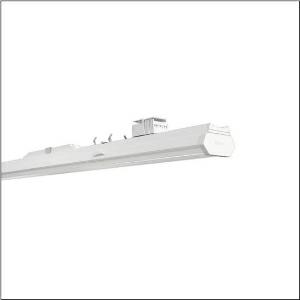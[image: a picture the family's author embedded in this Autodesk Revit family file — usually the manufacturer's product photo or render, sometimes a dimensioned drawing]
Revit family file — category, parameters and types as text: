
# Revit family: licross_r__11_protected_ho_51tp11cn4exs_0205
name_source: partatom
category: Lighting Fixtures
units: mm (PartAtom-declared; Revit-internal decimal feet)

## family parameters
Cut with Voids When Loaded = No
Host = Face
Light Source = No
Part Type = Normal
Room Calculation Point = No
Round Connector Dimension = Use Diameter
Shared = No

## types (1)
- --- (1 x LED, 14460 lm, 77.6 W, 4000K)
    Apparent Load = 78 VA
    CIE Flux Codes = 84 94 98 99 100
    Color Rendering = 80
    Color Temperature = 4000K
    Default Elevation = 1800 mm
    Description = Licross® 11 Protected HO, luminaire insert, of sheet steel, galvanised, coil coated, white, length: 1.500mm, width: 90mm, height: 101mm, LED rated luminous flux: 14.460lm, light colour: 840, control gear: ON/OFF Multilumen, CLOi, with plug, 3-pole, with phase selection, mains connection: 220..240V, AC, 50/60Hz, start of lifetime: 78W, end of service life: 87W, halogen-free wiring, primary light control with lens, of plastic, primary optical cover: cover, of PMMA, light emission: direct distribution, primary light characteristic: symmetric, protection rating (complete): IP64, insulation class (complete): insulation class I (protective earthing), certification: CE, ENEC, VDE, UKCA, protection symbol: D if used in an environment with conductive dust loads with corresponding accessories, impact resistance: IK06, permissible ambient temperature for indoor applications: -35..+35°C, corresponds to IFS (International Featured Standards) requirements for safety and quality in the food industry, reducing of maximum allowable ambient temperature of 5°C with ceiling mounting, LABS conformity tested according to VDMA 24364:2018-05, packaging unit: 1 piece
    Height = 92 mm
    Lamp = 1 x LED
    Lamp Light Flux = 14460 lm
    Lamp Power = 77.6 W
    Lamp count = 1
    Length = 1500 mm
    Luminous efficacy = 186 lm/W
    Manufacturer = Siteco
    ModVariant = No
    Model = 51TP11CN4EXS
    Mounting Place = Ceiling
    Mounting Type = Pendant
    Number of Poles = 1
    OnlyDefault = Yes
    Power Factor = 1
    Product Name = Licross® 11 Protected HO
    Product group = luminaire insert
    ProductGroupID = 902
    Protection Class = Protection class I
    Protection Degree = IP 64
    RLX_Detail_Level = 1
    RLX_Emergency_Light_Flux = 0 lm
    RLX_Emergency_Type = 0
    RLX_Emergency_Type_DB = No
    RlxData = <blob elided: 22105 chars, md5=fc189eae>
    Socket = socket
    Standby Power = 0 W
    System Light Flux = 14460 lm
    System Power = 78 W
    Type Comments = factory setting: luminous flux: 100 % | (A | C | E) | 181 mA
    Type Image = l_1256148.jpg
    URL = http://relux.com
    VarID = @adj_085808
    Voltage = 0 V
    Weight = 0.00 kg
    Width = 88 mm

## geometry (parser evidence)
native form markers: Blend x4, Sweep x12
no freeform markers — native parametric forms only
